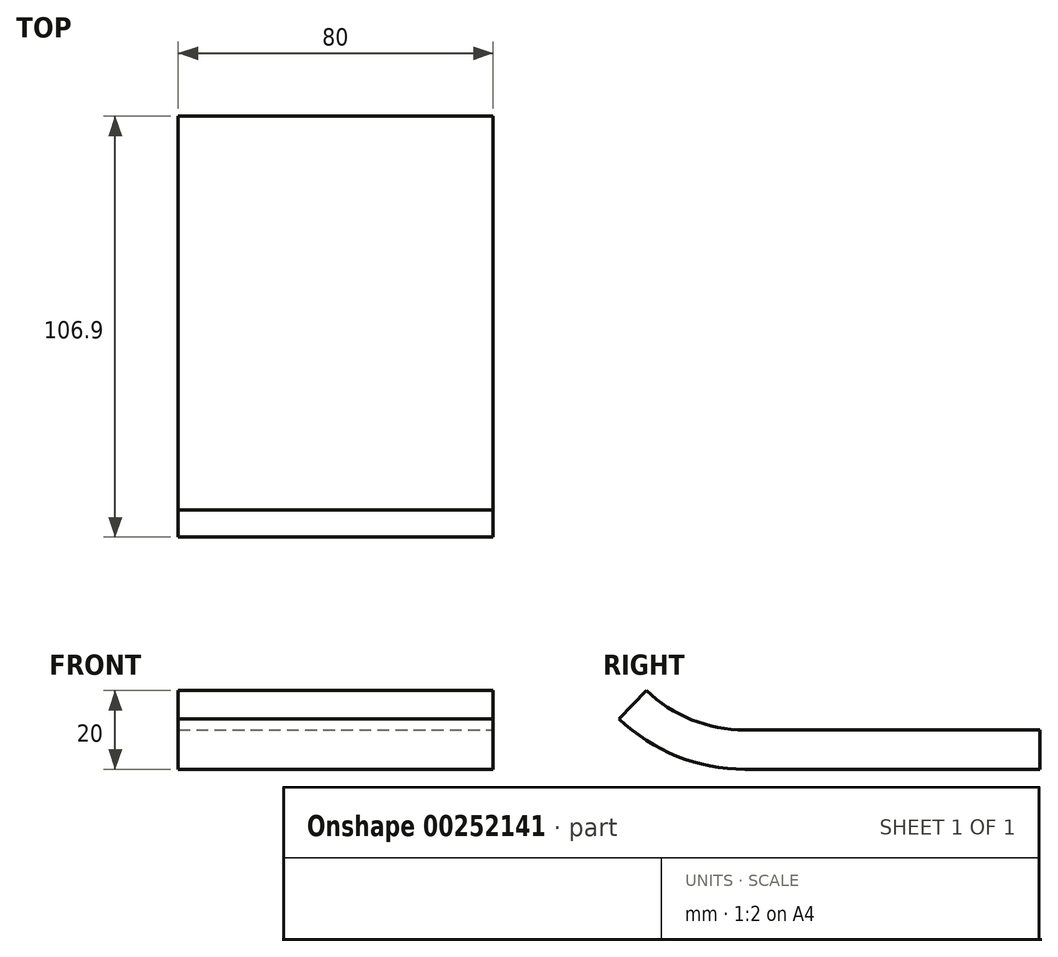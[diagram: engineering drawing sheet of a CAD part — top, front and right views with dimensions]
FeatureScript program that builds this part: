
annotation { "Feature Type Name" : "Feature", "Feature Type Description" : "" }
export const myFeature = defineFeature(function(context is Context, id is Id, definition is map)
    precondition{}
    {
        {
            var Q0;
            Q0=qCreatedBy(makeId("Right.planeOp"),FACE);
            var sketch = newSketch(context, id + "F0", { "sketchPlane" : qUnion([Q0])});
            skLineSegment(sketch, "E0.bottom", {"start": v(50, -5) * mm, "end": v(-25, -5) * mm});
            skLineSegment(sketch, "E0.top", {"start": v(50, 5) * mm, "end": v(-25, 5) * mm});
            skLineSegment(sketch, "E0.left", {"start": v(50, -5) * mm, "end": v(50, 5) * mm});
            skPoint(sketch, "E0.middle", {"position": v(0, 0) * mm});
            skPoint(sketch, "E1", {"position": v(0, 5) * mm});
            skArc(sketch, "E2", {"start": v(-50, 15) * mm, "mid": v(-38.46, 7.6) * mm, "end": v(-25, 5) * mm});
            skArc(sketch, "E3.0", {"start": v(-56.9, 7.76) * mm, "mid": v(-42.18, -1.7) * mm, "end": v(-25, -5) * mm});
            skLineSegment(sketch, "E4", {"start": v(-50, 15) * mm, "end": v(-56.9, 7.76) * mm});
            skPoint(sketch, "E5.orphan", {"position": v(-50, -5) * mm});
            skPoint(sketch, "E6.orphan", {"position": v(-50, 5) * mm});
            skSolve(sketch);
        }
        {
            var Q0;
            Q0=makeQuery(id+"F0.imprint","IMPRINT",FACE,{"disambiguationData":[TD([[makeQuery(id+"F0.imprint","IMPRINT",EDGE,{"derivedFrom":sQuery(id+"F0.wireOp",EDGE,"E0.bottom")}),-1.0]])]});
            extrude(context, id + "F1", {"entities" : qUnion([Q0]), "oppositeDirection" : true, "depth" : 80 * mm});
        }
    });
